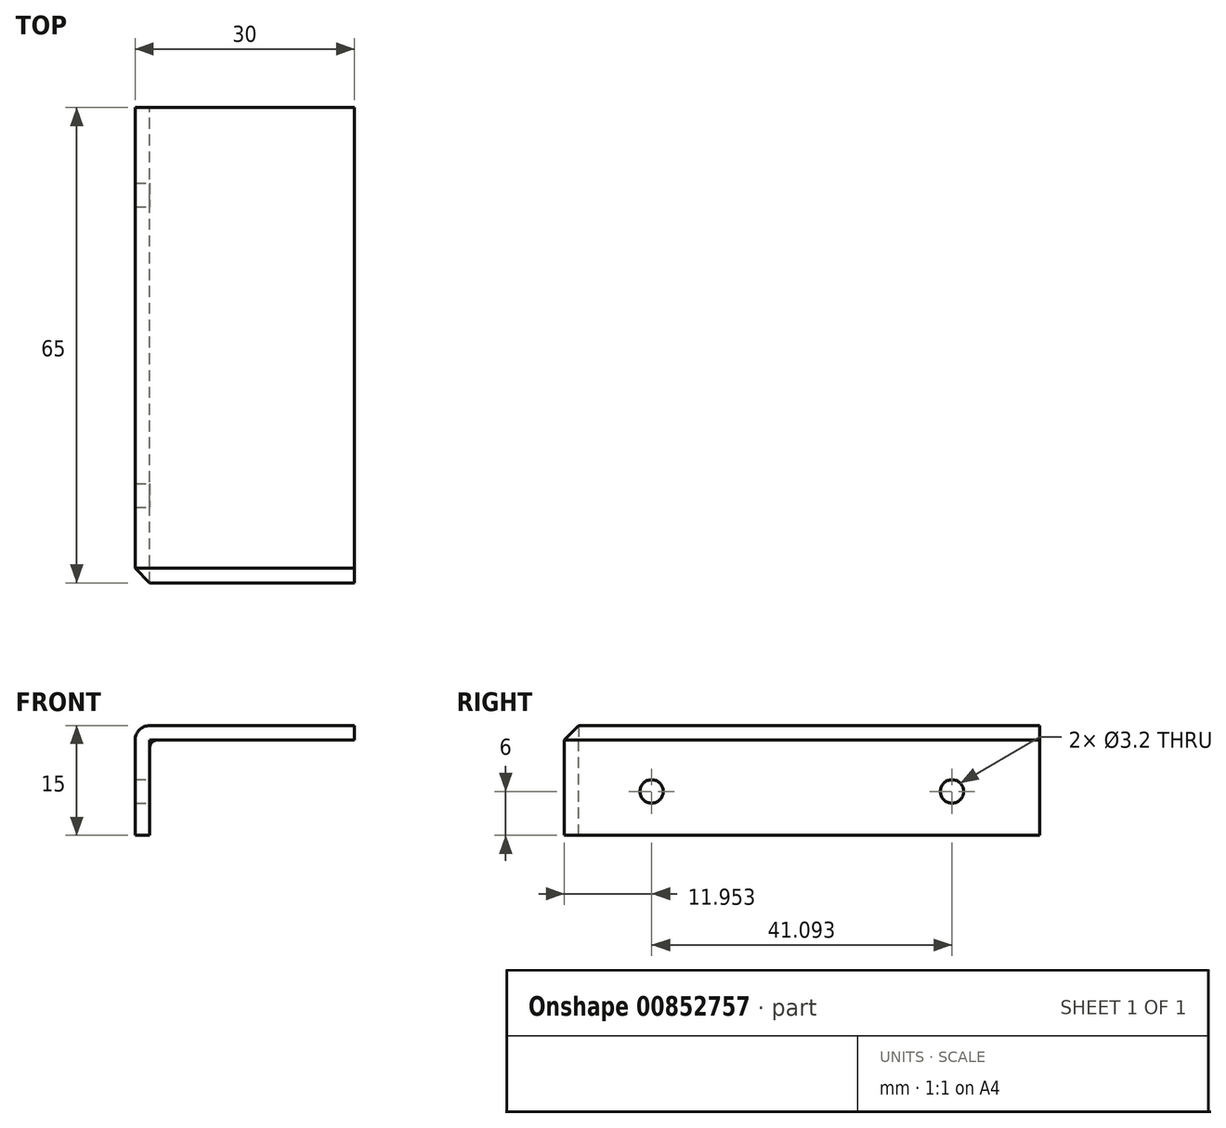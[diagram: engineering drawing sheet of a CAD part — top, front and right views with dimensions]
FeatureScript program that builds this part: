
annotation { "Feature Type Name" : "Feature", "Feature Type Description" : "" }
export const myFeature = defineFeature(function(context is Context, id is Id, definition is map)
    precondition{}
    {
        {
            var Q0;
            Q0=qCreatedBy(makeId("Front.planeOp"),FACE);
            var sketch = newSketch(context, id + "F0", { "sketchPlane" : qUnion([Q0])});
            skLineSegment(sketch, "E0", {"start": v(-16.85, -13.38) * mm, "end": v(-16.85, -0.38) * mm});
            skLineSegment(sketch, "E1", {"start": v(-14.85, 1.62) * mm, "end": v(13.15, 1.62) * mm});
            skLineSegment(sketch, "E2.0", {"start": v(-13.85, -0.38) * mm, "end": v(13.15, -0.38) * mm});
            skLineSegment(sketch, "E2.1", {"start": v(-14.85, -13.38) * mm, "end": v(-14.85, -1.38) * mm});
            skLineSegment(sketch, "E3", {"start": v(-16.85, -13.38) * mm, "end": v(-14.85, -13.38) * mm});
            skLineSegment(sketch, "E4", {"start": v(13.15, 1.62) * mm, "end": v(13.15, -0.38) * mm});
            skPoint(sketch, "E5.visualSharp", {"position": v(-16.85, 1.62) * mm});
            skArc(sketch, "E5.filletArc", {"start": v(-14.85, 1.62) * mm, "mid": v(-16.27, 1.03) * mm, "end": v(-16.85, -0.38) * mm});
            skArc(sketch, "E6.filletArc", {"start": v(-13.85, -0.38) * mm, "mid": v(-14.56, -0.67) * mm, "end": v(-14.85, -1.38) * mm});
            skSolve(sketch);
        }
        {
            var Q0;
            Q0=makeQuery(id+"F0.imprint","IMPRINT",FACE,{"disambiguationData":[TD([[makeQuery(id+"F0.imprint","IMPRINT",EDGE,{"derivedFrom":sQuery(id+"F0.wireOp",EDGE,"E0")}),-1.0]])]});
            extrude(context, id + "F1", {"entities" : qUnion([Q0]), "depth" : 65 * mm, "offsetDistance" : 25 * mm});
        }
        {
            var Q0;
            Q0=makeQuery(id+"F1.opExtrude","CAP_EDGE",EDGE,{"disambiguationData":[OSD([sQuery(id+"F0.wireOp",EDGE,"E0")])],"isStart":false});
            chamfer(context, id + "F2", {"entities" : qUnion([Q0]), "width" : 2 * mm, "tangentPropagation" : true});
        }
        {
            var Q0;
            Q0=makeQuery(id+"F1.opExtrude","SWEPT_FACE",FACE,{"disambiguationData":[OSD([sQuery(id+"F0.wireOp",EDGE,"E2.1")])]});
            var sketch = newSketch(context, id + "F3", { "sketchPlane" : qUnion([Q0])});
            skCircle(sketch, "E7", {"center": v(-53.05, -7.38) * mm, "radius": 1.6 * mm});
            skPoint(sketch, "E7.centerSnap0", {"position": v(-65, -7.38) * mm});
            skLineSegment(sketch, "E8", {"start": v(-32.5, 2.02) * mm, "end": v(-32.5, -13.38) * mm, "construction": true});
            skPoint(sketch, "E8.startSnap0", {"position": v(-32.5, -1.38) * mm});
            skCircle(sketch, "E9.MirrorC", {"center": v(-11.95, -7.38) * mm, "radius": 1.6 * mm});
            skSolve(sketch);
        }
        {
            var Q0;
            Q0 = qSketchRegion(id + "F3", true);
            extrude(context, id + "F4", {"entities" : qUnion([Q0]), "operationType" : NewBodyOperationType.REMOVE, "endBound" : BoundingType.UP_TO_NEXT, "oppositeDirection" : true, "depth" : 25 * mm, "offsetDistance" : 25 * mm});
        }
    });
